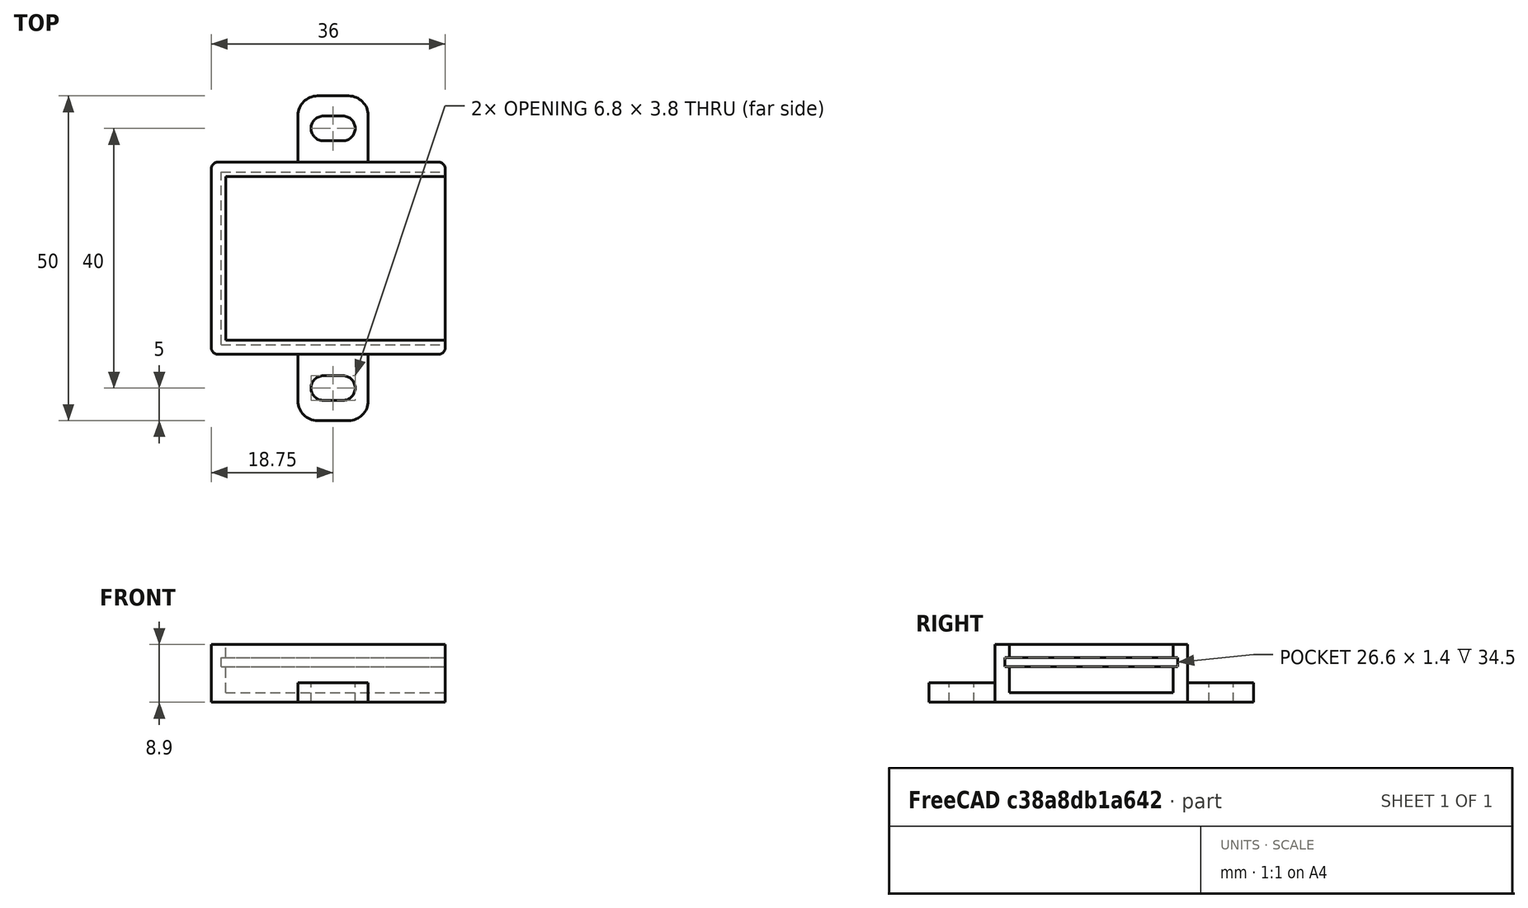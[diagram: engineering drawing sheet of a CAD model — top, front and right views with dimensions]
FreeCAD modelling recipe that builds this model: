
FCSTD DOCUMENT  (FreeCAD 0.18.4R)
Label: esp8622_esp201
License: FreeArt
LicenseURL: http://artlibre.org/licence/lal
objects: Part::Box×3, Part::MultiFuse×2, Spreadsheet::Sheet×1, Part::Fillet×1, Part::Feature×1, Part::Cut×1, App::Part×1
note: 8 computed .brp shape members not serialized (recipe doc carries the construction recipe); baked Part::Feature solids carry a one-line shape summary decoded from their .brp

FEATURE [Spreadsheet::Sheet] Spreadsheet  label="p"
  cells = A1=pcb_x; B1(pcb_x)=34.5; A2=pcb_y; B2(pcb_y)=26.6; A3=pcb_z; B3(pcb_z)=1.4; A4=pcb_under; B4(pcb_under)=4; A5=side_wall; B5(side_wall)=1.5; A6=pcb_side_lane; B6(pcb_side_lane)=0.7; A7=bottom_wall; B7(bottom_wall)=1.5; A8=pcb_above; B8(pcb_above)=2
FEATURE [Part::Box] Box  label="external cube"
  AttacherType = Attacher::AttachEngine3D
  Height = 8.9
  Length = 36
  Width = 29.6
  expr: Height = p.bottom_wall + p.pcb_under + p.pcb_z + p.pcb_above
  expr: Width = p.pcb_y + 2 * p.side_wall
  expr: Length = p.pcb_x + p.side_wall
FEATURE [Part::Box] Box006  label="internal cube"
  AttacherType = Attacher::AttachEngine3D
  Height = 7.4
  Length = 34.6
  Placement = pos=(2.2,2.2,1.5) rot=(0,0,1;0rad)
  Width = 25.2
  expr: Placement.Base.y = p.side_wall + p.pcb_side_lane
  expr: Placement.Base.x = p.side_wall + p.pcb_side_lane
  expr: Placement.Base.z = p.bottom_wall
  expr: Height = p.pcb_under + p.pcb_z + p.pcb_above
  expr: Width = p.pcb_y - 2 * p.pcb_side_lane
  expr: Length = p.pcb_x - 2 * p.pcb_side_lane + p.side_wall
FEATURE [Part::Box] Box007  label="pcb extract cube"
  AttacherType = Attacher::AttachEngine3D
  Height = 1.4
  Length = 34.5
  Placement = pos=(1.5,1.5,5.5) rot=(0,0,1;0rad)
  Width = 26.6
  expr: Placement.Base.y = p.side_wall
  expr: Placement.Base.x = p.side_wall
  expr: Length = p.pcb_x
  expr: Width = p.pcb_y
  expr: Placement.Base.z = p.bottom_wall + p.pcb_under
  expr: Height = p.pcb_z
FEATURE [Part::MultiFuse] Fusion  label="extract fusion"
  Shapes = -> [Box006,Box007]
FEATURE [Part::Fillet] Fillet  label="external fillet"
  Base = -> Box
  Edges = 4 edges r=1: [Edge1,Edge3,Edge5,Edge7]
FEATURE [Part::Feature] Cut002002  label="attach plane y dir002"
  shape: bbox 10.8 x 50 x 3 mm, 18 faces (baked)
FEATURE [Part::MultiFuse] Fusion001  label="solid fusion"
  Shapes = -> [Fillet,Cut002002]
FEATURE [Part::Cut] Cut  label="esp201 cut"
  Base = -> Fusion001
  Tool = -> Fusion
FEATURE [App::Part] Part  label="esp201 pcb box part"
  Group = -> [Box,Fillet,Fusion001,Fusion,Box007,Box006,Cut]
  Origin = -> Origin
